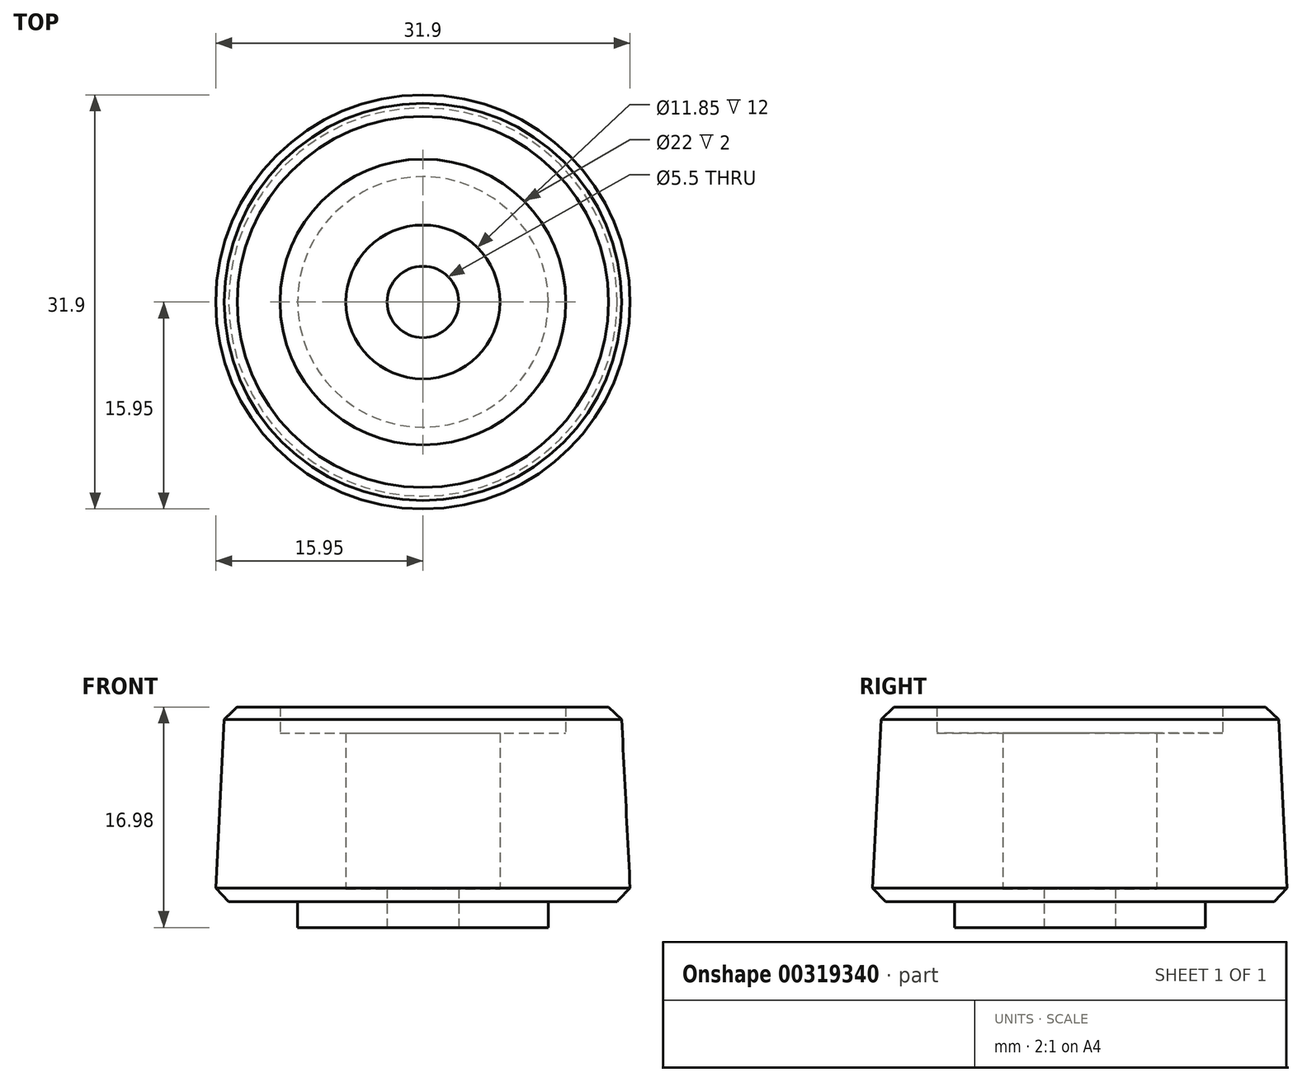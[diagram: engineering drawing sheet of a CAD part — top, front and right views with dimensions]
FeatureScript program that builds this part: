
annotation { "Feature Type Name" : "Feature", "Feature Type Description" : "" }
export const myFeature = defineFeature(function(context is Context, id is Id, definition is map)
    precondition{}
    {
        {
            var Q0;
            Q0=qCreatedBy(makeId("Right.planeOp"),FACE);
            var sketch = newSketch(context, id + "F0", { "sketchPlane" : qUnion([Q0])});
            skLineSegment(sketch, "E0", {"start": v(0, 2.98) * mm, "end": v(-5.92, 2.98) * mm});
            skLineSegment(sketch, "E1", {"start": v(-5.92, 2.98) * mm, "end": v(-5.92, 14.98) * mm});
            skLineSegment(sketch, "E2", {"start": v(-5.92, 14.98) * mm, "end": v(-11, 14.98) * mm});
            skLineSegment(sketch, "E3", {"start": v(-11, 14.98) * mm, "end": v(-11, 16.98) * mm});
            skLineSegment(sketch, "E4", {"start": v(-11, 16.98) * mm, "end": v(-15.25, 16.98) * mm});
            skLineSegment(sketch, "E5", {"start": v(-15.25, 16.98) * mm, "end": v(-16, 2) * mm});
            skLineSegment(sketch, "E6", {"start": v(-16, 2) * mm, "end": v(-9.65, 2) * mm});
            skLineSegment(sketch, "E7", {"start": v(-9.65, 2) * mm, "end": v(-9.65, 0) * mm});
            skLineSegment(sketch, "E8", {"start": v(-9.65, 0) * mm, "end": v(0, 0) * mm});
            skLineSegment(sketch, "E9", {"start": v(0, 0) * mm, "end": v(0, 2.98) * mm});
            skPoint(sketch, "E10", {"position": v(0, -3) * mm});
            skSolve(sketch);
        }
        {
            var Q0;
            Q0 = qSketchRegion(id + "F0", true);
            var Q1;
            Q1=sQuery(id+"F0.wireOp",EDGE,"E9");
            revolve(context, id + "F1", {"entities" : qUnion([Q0]), "axis" : qUnion([Q1]), "revolveType" : RevolveType.FULL});
        }
        {
            var Q0;
            Q0=makeQuery(id+"F1.opRevolve","SWEPT_FACE",FACE,{"disambiguationData":[OSD([sQuery(id+"F0.wireOp",EDGE,"E5")])]});
            chamfer(context, id + "F2", {"entities" : qUnion([Q0]), "width" : 1 * mm, "tangentPropagation" : true});
        }
        {
            var Q0;
            Q0=makeQuery(id+"F1.opRevolve","SWEPT_FACE",FACE,{"disambiguationData":[OSD([sQuery(id+"F0.wireOp",EDGE,"E8")])]});
            var sketch = newSketch(context, id + "F3", { "sketchPlane" : qUnion([Q0])});
            skPoint(sketch, "E11", {"position": v(0, 0) * mm});
            skSolve(sketch);
        }
        {
            var Q0;
            Q0=sQuery(id+"F3.wireOp",VERTEX,"E11");
            var Q1;
            Q1=makeQuery(id+"F1.opRevolve","SWEPT_BODY",BODY,{"disambiguationData":[OSD([sQuery(id+"F0.wireOp",EDGE,"E0"),sQuery(id+"F0.wireOp",EDGE,"E1"),sQuery(id+"F0.wireOp",EDGE,"E2"),sQuery(id+"F0.wireOp",EDGE,"E3"),sQuery(id+"F0.wireOp",EDGE,"E4"),sQuery(id+"F0.wireOp",EDGE,"E5"),sQuery(id+"F0.wireOp",EDGE,"E6"),sQuery(id+"F0.wireOp",EDGE,"E7"),sQuery(id+"F0.wireOp",EDGE,"E8"),sQuery(id+"F0.wireOp",EDGE,"E9")])]});
            hole(context, id + "F4", {"style" : HoleStyle.SIMPLE, "endStyle" : HoleEndStyle.THROUGH, "standardTappedOrClearance" : lookupTablePath({ "standard" : "ISO", "fit" : "Normal", "size" : "M5", "type" : "Clearance" }), "standardBlindInLast" : lookupTablePath({ "fit" : "Standard", "standard" : "ISO", "size" : "M5", "type" : "Clearance" }), "holeDiameter" : 5.5 * mm, "tappedDepth" : 12 * mm, "tapClearance" : 3, "locations" : qUnion([Q0]), "scope" : qUnion([Q1])});
        }
    });
